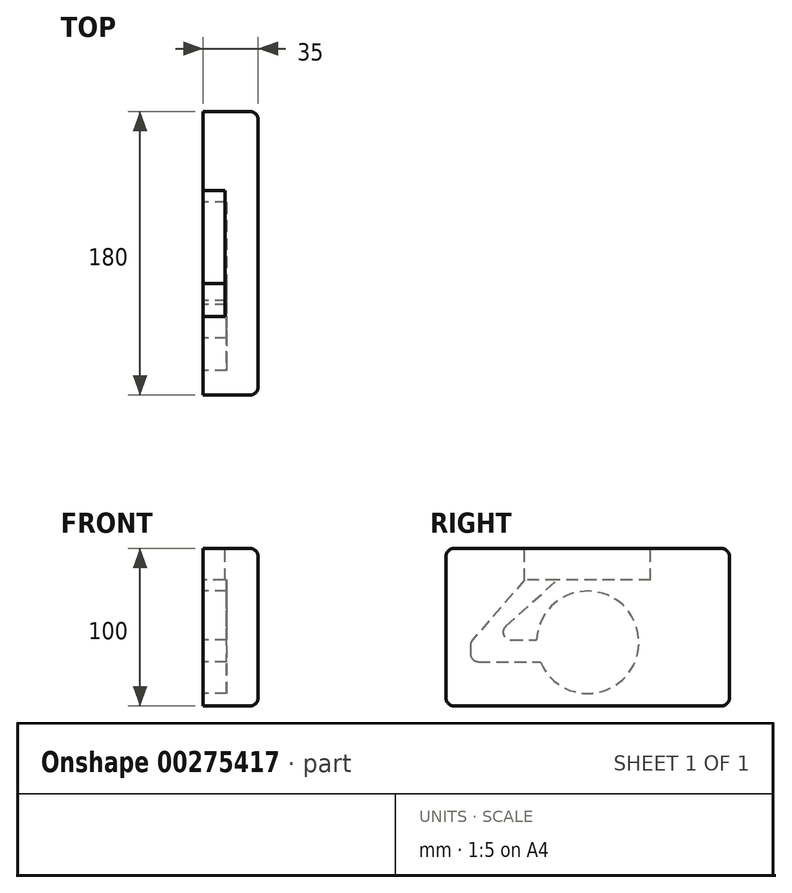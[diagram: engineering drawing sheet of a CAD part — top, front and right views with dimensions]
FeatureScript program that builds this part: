
annotation { "Feature Type Name" : "Feature", "Feature Type Description" : "" }
export const myFeature = defineFeature(function(context is Context, id is Id, definition is map)
    precondition{}
    {
        {
            var Q0;
            Q0=qCreatedBy(makeId("Right.planeOp"),FACE);
            var sketch = newSketch(context, id + "F0", { "sketchPlane" : qUnion([Q0])});
            skLineSegment(sketch, "E0.bottom", {"start": v(-111.97, 59.59) * mm, "end": v(58.03, 59.59) * mm});
            skLineSegment(sketch, "E0.top", {"start": v(-111.97, -40.41) * mm, "end": v(58.03, -40.41) * mm});
            skLineSegment(sketch, "E0.left", {"start": v(-116.97, 54.59) * mm, "end": v(-116.97, -35.41) * mm});
            skLineSegment(sketch, "E0.right", {"start": v(63.03, 54.59) * mm, "end": v(63.03, -35.41) * mm});
            skPoint(sketch, "E1.visualSharp", {"position": v(-116.97, -40.41) * mm});
            skArc(sketch, "E1.filletArc", {"start": v(-116.97, -35.41) * mm, "mid": v(-115.5, -38.95) * mm, "end": v(-111.97, -40.41) * mm});
            skPoint(sketch, "E2.visualSharp", {"position": v(63.03, -40.41) * mm});
            skArc(sketch, "E2.filletArc", {"start": v(58.03, -40.41) * mm, "mid": v(61.56, -38.95) * mm, "end": v(63.03, -35.41) * mm});
            skPoint(sketch, "E3.visualSharp", {"position": v(63.03, 59.59) * mm});
            skArc(sketch, "E3.filletArc", {"start": v(63.03, 54.59) * mm, "mid": v(61.56, 58.12) * mm, "end": v(58.03, 59.59) * mm});
            skPoint(sketch, "E4.visualSharp", {"position": v(-116.97, 59.59) * mm});
            skArc(sketch, "E4.filletArc", {"start": v(-111.97, 59.59) * mm, "mid": v(-115.5, 58.12) * mm, "end": v(-116.97, 54.59) * mm});
            skSolve(sketch);
        }
        {
            var Q0;
            Q0=makeQuery(id+"F0.imprint","IMPRINT",FACE,{"disambiguationData":[TD([[makeQuery(id+"F0.imprint","IMPRINT",EDGE,{"derivedFrom":sQuery(id+"F0.wireOp",EDGE,"E0.bottom")}),-1.0]])]});
            extrude(context, id + "F1", {"entities" : qUnion([Q0]), "depth" : 35 * mm, "offsetDistance" : 25 * mm});
        }
        {
            var Q0;
            Q0=makeQuery(id+"F1.opExtrude","SWEPT_FACE",FACE,{"disambiguationData":[OSD([sQuery(id+"F0.wireOp",EDGE,"E0.bottom")])]});
            var sketch = newSketch(context, id + "F2", { "sketchPlane" : qUnion([Q0])});
            skLineSegment(sketch, "E5.bottom", {"start": v(14, 13.03) * mm, "end": v(0, 13.03) * mm});
            skLineSegment(sketch, "E5.top", {"start": v(14, -66.97) * mm, "end": v(0, -66.97) * mm});
            skLineSegment(sketch, "E5.left", {"start": v(14, 13.03) * mm, "end": v(14, -66.97) * mm});
            skLineSegment(sketch, "E5.right", {"start": v(0, 13.03) * mm, "end": v(0, -66.97) * mm});
            skSolve(sketch);
        }
        {
            var Q0;
            Q0 = qSketchRegion(id + "F2", true);
            extrude(context, id + "F3", {"entities" : qUnion([Q0]), "operationType" : NewBodyOperationType.REMOVE, "oppositeDirection" : true, "depth" : 15 * mm, "offsetDistance" : 25 * mm});
        }
        {
            var Q0;
            Q0=makeQuery(id+"F1.opExtrude","CAP_FACE",FACE,{"disambiguationData":[OSD([sQuery(id+"F0.wireOp",EDGE,"E0.bottom"),sQuery(id+"F0.wireOp",EDGE,"E0.top"),sQuery(id+"F0.wireOp",EDGE,"E0.left"),sQuery(id+"F0.wireOp",EDGE,"E0.right")])],"isStart":true});
            var sketch = newSketch(context, id + "F4", { "sketchPlane" : qUnion([Q0])});
            skCircle(sketch, "E6", {"center": v(26.97, 0) * mm, "radius": 32.5 * mm});
            skSolve(sketch);
        }
        {
            var Q0;
            Q0 = qSketchRegion(id + "F4", true);
            extrude(context, id + "F5", {"entities" : qUnion([Q0]), "operationType" : NewBodyOperationType.REMOVE, "oppositeDirection" : true, "depth" : 15 * mm, "offsetDistance" : 25 * mm});
        }
        {
            var Q0;
            Q0=makeQuery(id+"F1.opExtrude","SWEPT_FACE",FACE,{"disambiguationData":[OSD([sQuery(id+"F0.wireOp",EDGE,"E0.bottom")])]});
            var sketch = newSketch(context, id + "F6", { "sketchPlane" : qUnion([Q0])});
            skLineSegment(sketch, "E7.bottom", {"start": v(15, 0) * mm, "end": v(0, 0) * mm});
            skLineSegment(sketch, "E7.top", {"start": v(15, -70) * mm, "end": v(0, -70) * mm});
            skLineSegment(sketch, "E7.left", {"start": v(15, 0) * mm, "end": v(15, -70) * mm});
            skLineSegment(sketch, "E7.right", {"start": v(0, 0) * mm, "end": v(0, -70) * mm});
            skSolve(sketch);
        }
        {
            var Q0;
            Q0=makeQuery(id+"F6.imprint","IMPRINT",FACE,{"disambiguationData":[TD([[makeQuery(id+"F6.imprint","IMPRINT",EDGE,{"derivedFrom":sQuery(id+"F6.wireOp",EDGE,"E7.bottom")}),1.0]])]});
            extrude(context, id + "F7", {"entities" : qUnion([Q0]), "operationType" : NewBodyOperationType.REMOVE, "oppositeDirection" : true, "depth" : 20 * mm});
        }
        {
            var Q0;
            Q0=makeQuery(id+"F3.boolean.opBoolean","COPY",FACE,{"derivedFrom":makeQuery(id+"F3.opExtrude","CAP_FACE",FACE,{"disambiguationData":[OSD([sQuery(id+"F2.wireOp",EDGE,"E5.bottom"),sQuery(id+"F2.wireOp",EDGE,"E5.top"),sQuery(id+"F2.wireOp",EDGE,"E5.left"),sQuery(id+"F2.wireOp",EDGE,"E5.right")])],"isStart":false})});
            extrude(context, id + "F8", {"entities" : qUnion([Q0]), "operationType" : NewBodyOperationType.REMOVE, "oppositeDirection" : true, "depth" : 5 * mm});
        }
        {
            var Q0;
            Q0=makeQuery(id+"F1.opExtrude","CAP_FACE",FACE,{"disambiguationData":[OSD([sQuery(id+"F0.wireOp",EDGE,"E0.bottom"),sQuery(id+"F0.wireOp",EDGE,"E0.top"),sQuery(id+"F0.wireOp",EDGE,"E0.left"),sQuery(id+"F0.wireOp",EDGE,"E0.right"),sQuery(id+"F0.wireOp",EDGE,"E1.filletArc"),sQuery(id+"F0.wireOp",EDGE,"E2.filletArc"),sQuery(id+"F0.wireOp",EDGE,"E3.filletArc"),sQuery(id+"F0.wireOp",EDGE,"E4.filletArc")])],"isStart":false});
            fillet(context, id + "F9", {"entities" : qUnion([Q0]), "radius" : 5 * mm, "tangentPropagation" : true, "allowEdgeOverflow" : false});
        }
        {
            var Q0;
            Q0=makeQuery(id+"F1.opExtrude","CAP_FACE",FACE,{"disambiguationData":[OSD([sQuery(id+"F0.wireOp",EDGE,"E0.bottom"),sQuery(id+"F0.wireOp",EDGE,"E0.top"),sQuery(id+"F0.wireOp",EDGE,"E0.left"),sQuery(id+"F0.wireOp",EDGE,"E0.right"),sQuery(id+"F0.wireOp",EDGE,"E1.filletArc"),sQuery(id+"F0.wireOp",EDGE,"E2.filletArc"),sQuery(id+"F0.wireOp",EDGE,"E3.filletArc"),sQuery(id+"F0.wireOp",EDGE,"E4.filletArc")])],"isStart":true});
            var sketch = newSketch(context, id + "F10", { "sketchPlane" : qUnion([Q0])});
            skLineSegment(sketch, "E8", {"start": v(66.97, 39.59) * mm, "end": v(100.14, 1.41) * mm});
            skLineSegment(sketch, "E9", {"start": v(101.37, -1.87) * mm, "end": v(101.37, -7.3) * mm});
            skLineSegment(sketch, "E10", {"start": v(96.37, -12.3) * mm, "end": v(57.05, -12.3) * mm});
            skLineSegment(sketch, "E11", {"start": v(75.67, 1.42) * mm, "end": v(59.44, 1.42) * mm});
            skLineSegment(sketch, "E12", {"start": v(79.02, 10.13) * mm, "end": v(46.27, 39.59) * mm});
            skPoint(sketch, "E13.visualSharp", {"position": v(101.37, -12.3) * mm});
            skArc(sketch, "E13.filletArc", {"start": v(96.37, -12.3) * mm, "mid": v(99.9, -10.84) * mm, "end": v(101.37, -7.3) * mm});
            skPoint(sketch, "E14.visualSharp", {"position": v(101.37, 0) * mm});
            skArc(sketch, "E14.filletArc", {"start": v(101.37, -1.87) * mm, "mid": v(101.05, -0.12) * mm, "end": v(100.14, 1.41) * mm});
            skPoint(sketch, "E15.visualSharp", {"position": v(88.7, 1.42) * mm});
            skArc(sketch, "E15.filletArc", {"start": v(75.67, 1.42) * mm, "mid": v(80.34, 4.63) * mm, "end": v(79.02, 10.13) * mm});
            skSolve(sketch);
        }
        {
            var Q0;
            {var subQ2=sQuery(id+"F10.wireOp",EDGE,"E8");Q0=makeQuery(id+"F10.imprint","IMPRINT",FACE,{"disambiguationData":[TD([[makeQuery(id+"F10.imprint","IMPRINT",EDGE,{"derivedFrom":subQ2}),-1.0]])]});}
            extrude(context, id + "F11", {"entities" : qUnion([Q0]), "operationType" : NewBodyOperationType.REMOVE, "oppositeDirection" : true, "depth" : 15 * mm, "offsetDistance" : 25 * mm});
        }
    });
